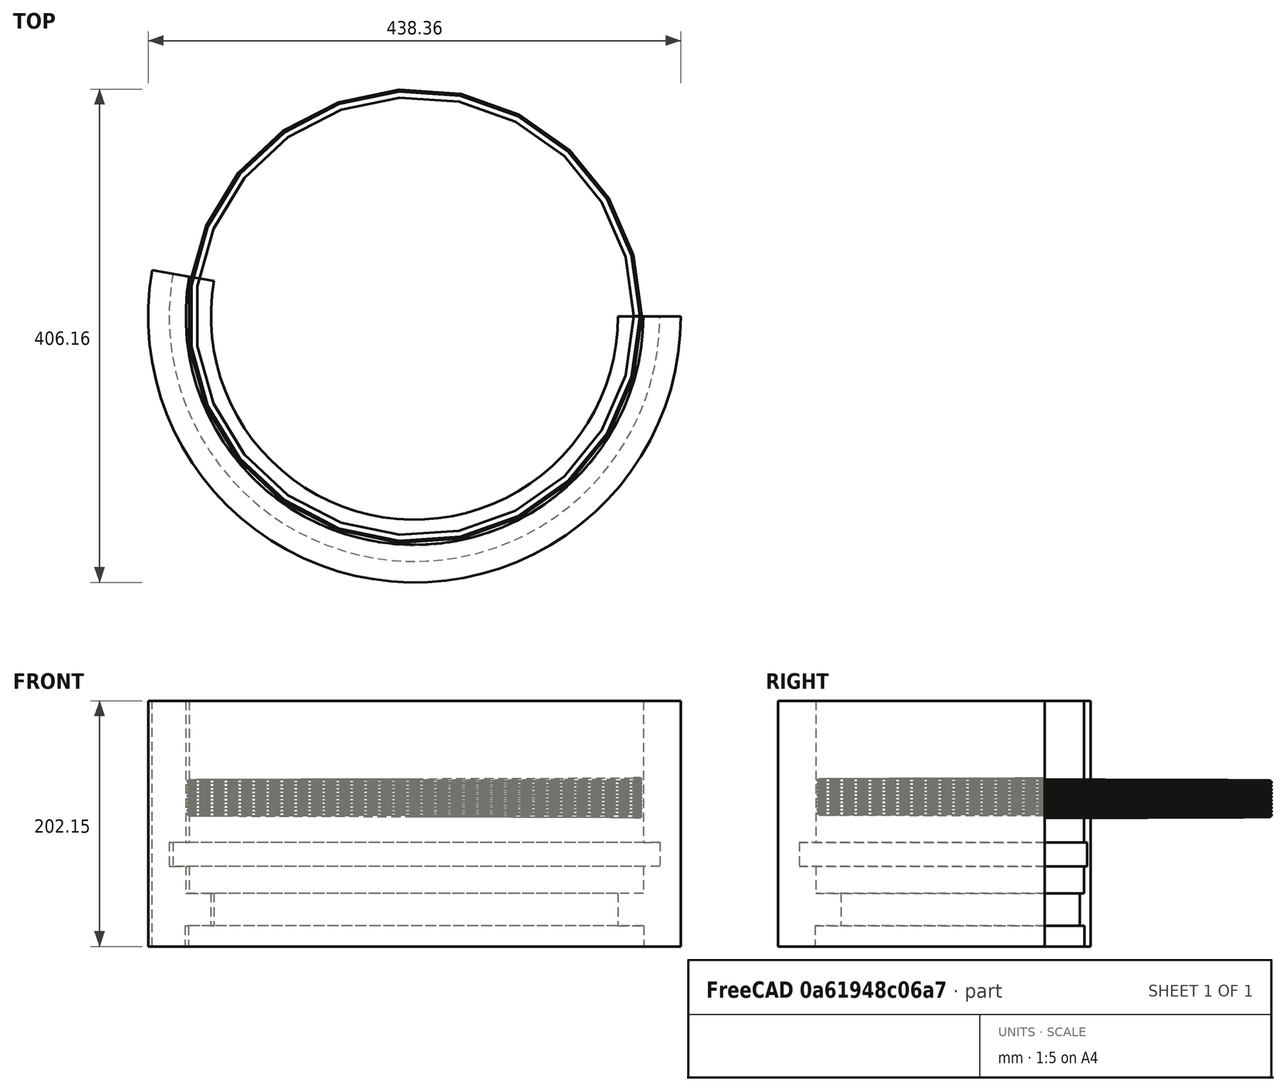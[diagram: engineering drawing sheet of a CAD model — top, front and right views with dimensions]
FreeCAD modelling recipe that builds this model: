
FCSTD DOCUMENT  (FreeCAD 0.18.4R)
Label: combined
License: All rights reserved
LicenseURL: http://en.wikipedia.org/wiki/All_rights_reserved
objects: Sketcher::SketchObject×2, PartDesign::Body×2, Spreadsheet::Sheet×1, Part::Helix×1, PartDesign::AdditivePipe×1, PartDesign::Revolution×1, TechDraw::DrawSVGTemplate×1, TechDraw::DrawViewPart×1, TechDraw::DrawPage×1
note: 9 computed .brp shape members not serialized (recipe doc carries the construction recipe); baked Part::Feature solids carry a one-line shape summary decoded from their .brp

FEATURE [Spreadsheet::Sheet] Spreadsheet  label="Parameters"
  cells = A1=oring_r1; B1(oring_r1)=185; A2=oring_r2; B2(oring_r2)=200; A3=oring_r3; B3(oring_r3)=220; A4=oring_h1; B4(oring_h1)=10; A5=oring_h2; B5(oring_h2)=20; A6=thread_dmin; B6(thread_dmin)=180; A7=thread_dpitch; B7(thread_dpitch)=190; A8=thread_dmax; B8(thread_dmax)==oring_r2; A9=thread_pitch; B9(thread_pitch)=3; A10=a; B10(a)=5; A11=b; B11(b)=8
FEATURE [Part::Helix] Helix001
  Angle = 0
  AttacherType = Attacher::AttachEngine3D
  Height = 30
  LocalCoord = 0
  Pitch = 3
  Radius = 180
  Style = 1
FEATURE [Sketcher::SketchObject] Sketch
  ExternalGeometry = -> [Helix001]
  MapMode = 7
  Placement = pos=(180,-1.353e-13,0) rot=(1,0,0;1.57345rad)
  Support = -> [Helix001]
  expr: Constraints[6] = Parameters.a
  expr: Constraints[7] = Parameters.a
  expr: Constraints[13] = Parameters.thread_pitch
  sketch-geometry (6):
    g0: LineSegment StartX=0.340932 StartY=-0.00288345 StartZ=0 EndX=5.34093 EndY=-0.00288345 EndZ=0
    g1: LineSegment StartX=5.34093 StartY=-0.00288345 StartZ=0 EndX=6.98288 EndY=1.04055 EndZ=0
    g2: LineSegment StartX=6.98288 StartY=1.04055 StartZ=0 EndX=6.98288 EndY=2.14002 EndZ=0
    g3: LineSegment StartX=6.98288 StartY=2.14002 StartZ=0 EndX=5.34093 EndY=2.99712 EndZ=0
    g4: LineSegment StartX=5.34093 StartY=2.99712 StartZ=0 EndX=0.340932 EndY=2.99712 EndZ=0
    g5: LineSegment StartX=0.340932 StartY=2.99712 StartZ=0 EndX=0.340932 EndY=-0.00288345 EndZ=0
  constraints (14):
    c: Coincident(g0,g1)
    c: Coincident(g1,g2)
    c: Coincident(g2,g3)
    c: Coincident(g3,g4)
    c: Coincident(g4,g5)
    c: Coincident(g5,g0)
    c: DistanceX(g4,g4) = 5
    c: DistanceX(g0,g0) = 5
    c: Horizontal(g0)
    c: Horizontal(g4)
    c: Vertical(g5)
    c: Vertical(g2)
    c: Angle(g3,g1) = 1.0472
    c: DistanceY(g5,g5) = 3
FEATURE [PartDesign::AdditivePipe] AdditivePipe
  AuxilleryCurvelinear = true
  AuxillerySpineTangent = false
  Binormal = (0,0,0)
  Mode = 2
  Profile = -> Sketch
  Spine = -> Helix001
  SpineTangent = false
  Transformation = 0
  Transition = 0
FEATURE [PartDesign::Body] Body  label="Threaded_retainer"
  Group = -> [Sketch,AdditivePipe]
  Origin = -> Origin
  Tip = -> AdditivePipe
FEATURE [Sketcher::SketchObject] Sketch001
  MapMode = 5
  Placement = pos=(0,0,0) rot=(1,0,0;1.5708rad)
  Support = -> [XZ_Plane001]
  sketch-geometry (12):
    g0: LineSegment StartX=188.172 StartY=93.3041 StartZ=0 EndX=188.172 EndY=-23.1265 EndZ=0
    g1: LineSegment StartX=188.172 StartY=-23.1265 StartZ=0 EndX=201.852 EndY=-23.1265 EndZ=0
    g2: LineSegment StartX=201.852 StartY=-23.1265 StartZ=0 EndX=201.852 EndY=-42.8863 EndZ=0
    g3: LineSegment StartX=201.852 StartY=-42.8863 StartZ=0 EndX=188.172 EndY=-42.8863 EndZ=0
    g4: LineSegment StartX=188.172 StartY=-42.8863 StartZ=0 EndX=188.172 EndY=-65.078 EndZ=0
    g5: LineSegment StartX=188.172 StartY=-65.078 StartZ=0 EndX=167.5 EndY=-65.078 EndZ=0
    g6: LineSegment StartX=167.5 StartY=-65.078 StartZ=0 EndX=167.5 EndY=-91.8297 EndZ=0
    g7: LineSegment StartX=167.5 StartY=-91.8297 StartZ=0 EndX=188.78 EndY=-91.8297 EndZ=0
    g8: LineSegment StartX=188.78 StartY=-91.8297 StartZ=0 EndX=188.78 EndY=-108.853 EndZ=0
    g9: LineSegment StartX=188.78 StartY=-108.853 StartZ=0 EndX=219.18 EndY=-108.853 EndZ=0
    g10: LineSegment StartX=219.18 StartY=-108.853 StartZ=0 EndX=219.18 EndY=93.3041 EndZ=0
    g11: LineSegment StartX=219.18 StartY=93.3041 StartZ=0 EndX=188.172 EndY=93.3041 EndZ=0
  constraints (24):
    c: Coincident(g0,g1)
    c: Coincident(g1,g2)
    c: Coincident(g2,g3)
    c: Coincident(g3,g4)
    c: Coincident(g4,g5)
    c: Coincident(g5,g6)
    c: Coincident(g6,g7)
    c: Coincident(g7,g8)
    c: Coincident(g8,g9)
    c: Coincident(g9,g10)
    c: Coincident(g10,g11)
    c: Coincident(g11,g0)
    c: Vertical(g0)
    c: Vertical(g10)
    c: Vertical(g2)
    c: Vertical(g4)
    c: Vertical(g6)
    c: Vertical(g8)
    c: Horizontal(g11)
    c: Horizontal(g1)
    c: Horizontal(g3)
    c: Horizontal(g5)
    c: Horizontal(g7)
    c: Horizontal(g9)
FEATURE [PartDesign::Revolution] Revolution
  Angle = 170
  Axis = (0,2e-16,1)
  Base = (0,0,0)
  Placement = pos=(0,0,0) rot=(1,0,0;1.5708rad)
  Profile = -> Sketch001
  ReferenceAxis = -> Revolution
  Reversed = true
FEATURE [PartDesign::Body] Body001  label="Cell"
  Group = -> [Sketch001,Revolution]
  Origin = -> Origin001
  Tip = -> Revolution
FEATURE [TechDraw::DrawSVGTemplate] Template
  EditableTexts = Designed_by_Name=Designed by Name; Drawing_number=Drawing number; FC-Date=Date; FC-SC=Scale; FC-SH=Sheet; FC-Title=Title; Subtitle=Subtitle; Weight=Weight
  Height = 210
  Orientation = 1
  Width = 297
FEATURE [TechDraw::DrawViewPart] View
  CoarseView = false
  Direction = (-0.577,0.577,0.577)
  Focus = 100
  HardHidden = false
  IsoCount = 0
  IsoHidden = false
  IsoVisible = false
  LockPosition = false
  Perspective = false
  Rotation = 0
  Scale = 0.2
  ScaleType = 0
  SeamHidden = false
  SeamVisible = false
  SmoothHidden = false
  SmoothVisible = false
  Source = -> [Body,Body001]
  X = 67.0036
  Y = 146.387
  expr: Scale = 0.2
FEATURE [TechDraw::DrawPage] Page
  KeepUpdated = true
  ProjectionType = 1
  Template = -> Template
  Views = -> [View]
